# Revit family: AVRORA
name_source: partatom
category: Осветительные приборы
units: mm (PartAtom-declared; Revit-internal decimal feet)

## family parameters
Всегда вертикально = Нет
Источник света = Да
На основе рабочей плоскости = Нет
Общий = Нет
При загрузке вырезать с полостями = Нет
Размер круглого соединителя = Использовать диаметр
Тип детали = Нормальный
Точка расчета площади = Да

## types (10) — shared parameters
ADSK_Единица измерения = шт.
ADSK_Завод-изготовитель = ЗАО «Центрстройсвет»
ADSK_Классификация нагрузок = Прочее
ADSK_Количество фаз = 1
ADSK_Количество фаз числовое = 1
ADSK_Коэффициент мощности = 0.92
ADSK_Масса = 2.7
ADSK_Напряжение = 230 В
ADSK_Номинальная мощность = 32 Вт
ADSK_Полная мощность = 35 В·А
ADSK_Ток = 0 А
URL = http://csvt.ru
Видимая форма излучения при визуализации = Да
Высота = 25 мм
Изготовитель = ЗАО «Центрстройсвет»
Материал светильника = RAL 9006
Материал стекла = RAL светящийся
Светофильтр = 16777215
Смещение цветовой температуры при затухании лампы = <Нет>
Угол наклона = 90.00°

## per-type parameters (varying)
| type | ADSK_Код изделия | ADSK_Наименование | ADSK_Обозначение | Длина | Излучение по длине прямоугольника | Излучение по ширине прямоугольника | Файл фотометрической сетки | Ширина |
| AVRORA-32/opal-sand 595x595х25 (IP20, 4000К) | РУ000003200 | Встраиваемый светодиодный светильник AVRORA-32/opal-sand 595x595х25 (IP20, 4000К) | AVRORA-32/opal-sand 595x595х25 (IP20, 4000К) | 595 мм | 555 мм | 555 мм | Светильник AVRORA-32  OPAL-SAND-(595x595).ies | 595 мм |
| AVRORA-32/opal-sand 595x595х25 (IP20, 4000К) с БАП на 1 час | ЦБ000008826 | Встраиваемый светодиодный светильник AVRORA-32/opal-sand 595x595х25 (IP20, 4000К) с БАП на 1 час | AVRORA-32/opal-sand 595x595х25 (IP20, 4000К) | 595 мм | 555 мм | 555 мм | Светильник AVRORA-32  OPAL-SAND-(595x595).ies | 595 мм |
| AVRORA-32/opal-sand 595x595х25 (IP20, 4000К) с БАП на 3 часа | ЦБ000008827 | Встраиваемый светодиодный светильник AVRORA-32/opal-sand 595x595х25 (IP20, 4000К) с БАП на 3 часа | AVRORA-32/opal-sand 595x595х25 (IP20, 4000К) | 595 мм | 555 мм | 555 мм | Светильник AVRORA-32  OPAL-SAND-(595x595).ies | 595 мм |
| AVRORA-32/prisma 595x595х25 (IP20, 4000К) | ЦБ000008869 | Встраиваемый светодиодный светильник AVRORA-32/prisma 595x595х25 (IP20, 4000К) | AVRORA-32/prisma 595x595х25 (IP20, 4000К) | 595 мм | 555 мм | 555 мм | Светильник AVRORA-32 PRISMA-(595x595).ies | 595 мм |
| AVRORA-32/prisma 595x595х25 (IP20, 4000К) с БАП на 1 час | ЦБ000008871 | Встраиваемый светодиодный светильник AVRORA-32/prisma 595x595х25 (IP20, 4000К) с БАП на 1 час | AVRORA-32/prisma 595x595х25 (IP20, 4000К) | 595 мм | 555 мм | 555 мм | Светильник AVRORA-32 PRISMA-(595x595).ies | 595 мм |
| AVRORA-32/prisma 595x595х25 (IP20, 4000К) с БАП на 3 часа | ЦБ000008872 | Встраиваемый светодиодный светильник AVRORA-32/prisma 595x595х25 (IP20, 4000К) с БАП на 3 часа | AVRORA-32/prisma 595x595х25 (IP20, 4000К) | 595 мм | 555 мм | 555 мм | Светильник AVRORA-32 PRISMA-(595x595).ies | 595 мм |
| AVRORA-32/opal-sand 603х603х25 (IP20, 4000К, в грильято) | ЦБ000009020 | Встраиваемый светодиодный светильник AVRORA-32/opal-sand 603х603х25 (IP20, 4000К, в грильято) | AVRORA-32/opal-sand 603х603х25 (IP20, 4000К, в грильято) | 603 мм | 563 мм | 563 мм | Светильник AVRORA-32  OPAL-SAND-(595x595).ies | 603 мм |
| AVRORA-32/prisma 603х603х25 (IP20, 4000К, в грильято) | ЦБ000009021 | Встраиваемый светодиодный светильник AVRORA-32/prisma 603х603х25 (IP20, 4000К, в грильято) | AVRORA-32/prisma 603х603х25 (IP20, 4000К, в грильято) | 603 мм | 563 мм | 563 мм | Светильник AVRORA-32 PRISMA-(595x595).ies | 603 мм |
| AVRORA-32/opal-sand 603х603х25 (IP20, 5000К, в грильято) | ЦБ000009313 | Встраиваемый светодиодный светильник AVRORA-32/opal-sand 603х603х25 (IP20, 5000К, в грильято) | AVRORA-32/opal-sand 603х603х25 (IP20, 5000К, в грильято) | 603 мм | 563 мм | 563 мм | Светильник AVRORA-32  OPAL-SAND-(595x595).ies | 603 мм |
| AVRORA-32/prisma 603х603х25 (IP20, 5000К, в грильято) | ЦБ000009314 | Встраиваемый светодиодный светильник AVRORA-32/prisma 603х603х25 (IP20, 5000К, в грильято) | AVRORA-32/prisma 603х603х25 (IP20, 5000К, в грильято) | 603 мм | 563 мм | 563 мм | Светильник AVRORA-32 PRISMA-(595x595).ies | 603 мм |
